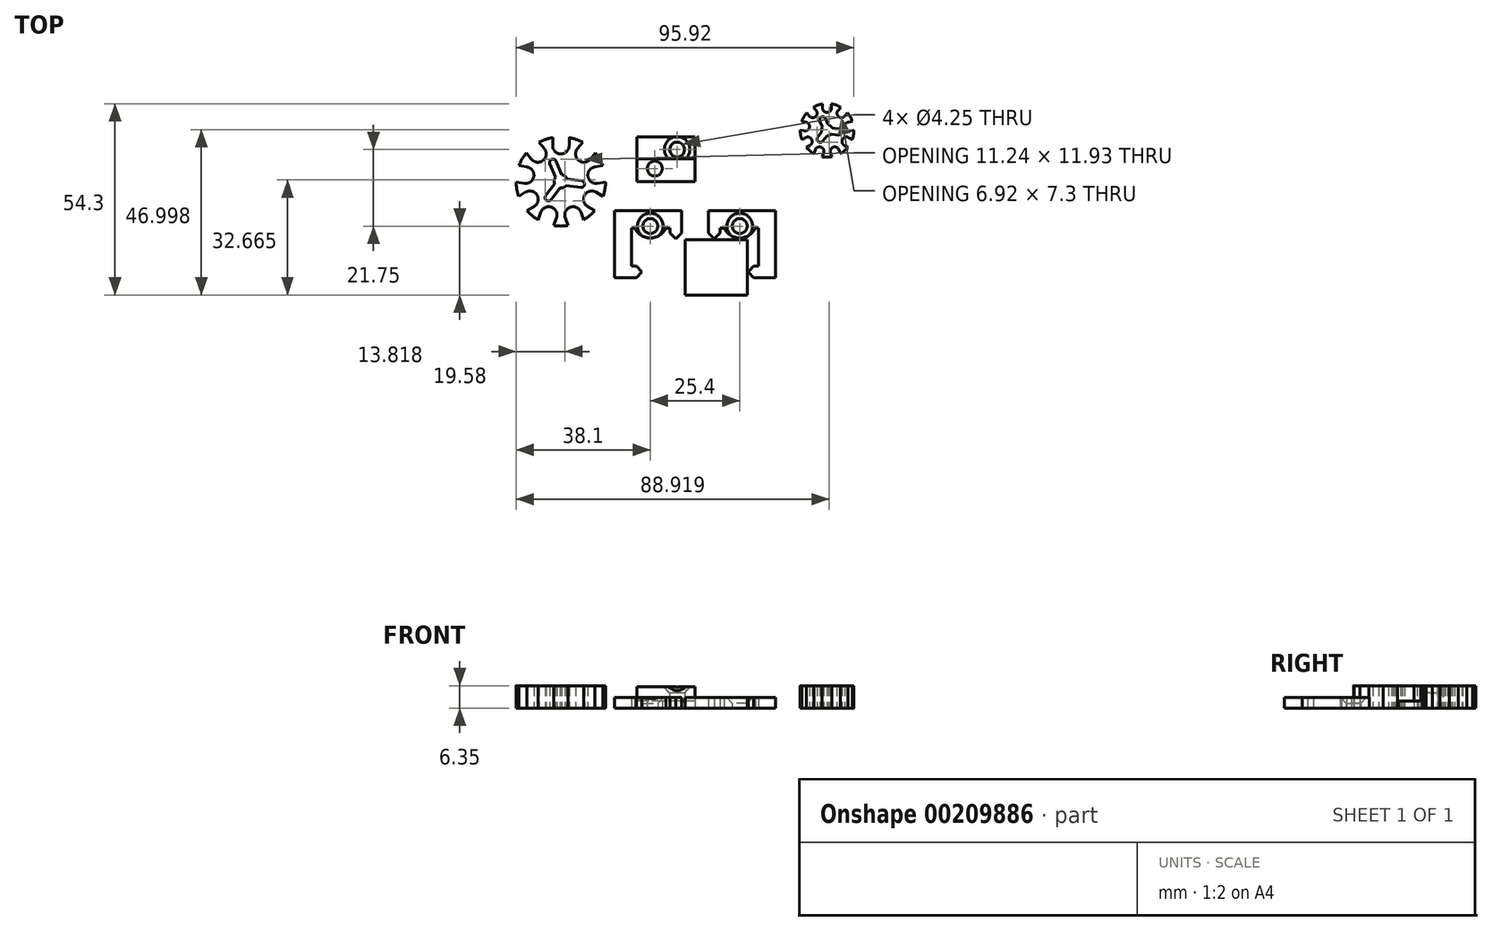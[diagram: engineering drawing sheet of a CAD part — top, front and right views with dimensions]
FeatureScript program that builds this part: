
annotation { "Feature Type Name" : "Feature", "Feature Type Description" : "" }
export const myFeature = defineFeature(function(context is Context, id is Id, definition is map)
    precondition{}
    {
        {
            var Q0;
            Q0=qCreatedBy(makeId("Top.planeOp"),FACE);
            var sketch = newSketch(context, id + "F0", { "sketchPlane" : qUnion([Q0])});
            skLineSegment(sketch, "E0.bottom", {"start": v(0, 0) * mm, "end": v(-16.51, 0) * mm});
            skLineSegment(sketch, "E0.top", {"start": v(0, 12.7) * mm, "end": v(-16.51, 12.7) * mm});
            skLineSegment(sketch, "E0.left", {"start": v(0, 0) * mm, "end": v(0, 12.7) * mm});
            skLineSegment(sketch, "E0.right", {"start": v(-16.51, 0) * mm, "end": v(-16.51, 12.7) * mm});
            skCircle(sketch, "E1", {"center": v(-11.43, 3.65) * mm, "radius": 2.12 * mm});
            skCircle(sketch, "E2", {"center": v(-5.08, 9.05) * mm, "radius": 2.12 * mm});
            skLineSegment(sketch, "E3", {"start": v(-11.43, 3.65) * mm, "end": v(-5.08, 3.65) * mm, "construction": true});
            skLineSegment(sketch, "E4", {"start": v(-5.08, 3.65) * mm, "end": v(-5.08, 9.05) * mm, "construction": true});
            skLineSegment(sketch, "E5", {"start": v(-16.51, 6.35) * mm, "end": v(0, 6.35) * mm, "construction": true});
            skPoint(sketch, "E6", {"position": v(-5.08, 6.35) * mm});
            skLineSegment(sketch, "E7", {"start": v(-5.08, 3.65) * mm, "end": v(0, 3.65) * mm, "construction": true});
            skLineSegment(sketch, "E8", {"start": v(-5.08, 3.65) * mm, "end": v(-5.08, 0) * mm, "construction": true});
            skLineSegment(sketch, "E9", {"start": v(-5.08, 9.05) * mm, "end": v(-5.08, 12.7) * mm, "construction": true});
            skPoint(sketch, "E10", {"position": v(-8.26, 3.65) * mm});
            skPoint(sketch, "E11", {"position": v(-8.26, 0) * mm});
            skSolve(sketch);
        }
        {
            var Q0;
            Q0 = qSketchRegion(id + "F0", true);
            extrude(context, id + "F1", {"entities" : qUnion([Q0]), "depth" : 2 * mm});
        }
        {
            var Q0;
            Q0=makeQuery(id+"F1.opExtrude","CAP_FACE",FACE,{"disambiguationData":[OSD([sQuery(id+"F0.wireOp",EDGE,"E0.bottom"),sQuery(id+"F0.wireOp",EDGE,"E0.top"),sQuery(id+"F0.wireOp",EDGE,"E0.left"),sQuery(id+"F0.wireOp",EDGE,"E0.right"),sQuery(id+"F0.wireOp",EDGE,"E1"),sQuery(id+"F0.wireOp",EDGE,"E2")])],"isStart":false});
            var sketch = newSketch(context, id + "F2", { "sketchPlane" : qUnion([Q0])});
            skLineSegment(sketch, "E12.bottom", {"start": v(0, 0) * mm, "end": v(-16.51, 0) * mm});
            skLineSegment(sketch, "E12.top", {"start": v(0, 6.4) * mm, "end": v(-16.51, 6.4) * mm});
            skLineSegment(sketch, "E12.left", {"start": v(0, 0) * mm, "end": v(0, 6.4) * mm});
            skLineSegment(sketch, "E12.right", {"start": v(-16.51, 0) * mm, "end": v(-16.51, 6.4) * mm});
            skCircle(sketch, "E13", {"center": v(-11.43, 3.65) * mm, "radius": 1.48 * mm, "construction": true});
            skSolve(sketch);
        }
        {
            var Q0;
            {var subQ2=sQuery(id+"F2.wireOp",EDGE,"E12.top");Q0=makeQuery(id+"F2.imprint","IMPRINT",FACE,{"disambiguationData":[TD([[makeQuery(id+"F2.imprint","IMPRINT",EDGE,{"derivedFrom":subQ2}),-1.0]])]});}
            extrude(context, id + "F3", {"entities" : qUnion([Q0]), "operationType" : NewBodyOperationType.ADD, "depth" : 4 * mm});
        }
        {
            var Q0;
            Q0=qCreatedBy(makeId("Top.planeOp"),FACE);
            var sketch = newSketch(context, id + "F4", { "sketchPlane" : qUnion([Q0])});
            skCircle(sketch, "E14", {"center": v(12.7, -12.7) * mm, "radius": 2.12 * mm});
            skLineSegment(sketch, "E15.bottom", {"start": v(14.83, -16.51) * mm, "end": v(-2.84, -16.5) * mm});
            skLineSegment(sketch, "E15.top", {"start": v(14.83, -32.28) * mm, "end": v(-2.84, -32.28) * mm});
            skLineSegment(sketch, "E15.left", {"start": v(14.83, -16.5) * mm, "end": v(14.83, -32.28) * mm});
            skLineSegment(sketch, "E15.right", {"start": v(-2.84, -16.51) * mm, "end": v(-2.84, -32.28) * mm});
            skLineSegment(sketch, "E16", {"start": v(22.9, -8.25) * mm, "end": v(22.9, -27.3) * mm});
            skLineSegment(sketch, "E17", {"start": v(22.9, -27.3) * mm, "end": v(16.68, -27.3) * mm});
            skLineSegment(sketch, "E18", {"start": v(16.68, -27.3) * mm, "end": v(15.08, -25.7) * mm});
            skLineSegment(sketch, "E19", {"start": v(15.08, -25.7) * mm, "end": v(16.68, -24.1) * mm});
            skLineSegment(sketch, "E20", {"start": v(16.68, -24.1) * mm, "end": v(18.08, -24.1) * mm});
            skLineSegment(sketch, "E21", {"start": v(18.08, -24.1) * mm, "end": v(18.08, -13.26) * mm});
            skLineSegment(sketch, "E22", {"start": v(18.08, -13.26) * mm, "end": v(7.05, -13.26) * mm});
            skLineSegment(sketch, "E23", {"start": v(3.85, -17.14) * mm, "end": v(3.85, -8.25) * mm});
            skLineSegment(sketch, "E24", {"start": v(7.05, -13.26) * mm, "end": v(3.85, -13.26) * mm, "construction": true});
            skLineSegment(sketch, "E25", {"start": v(18.08, -24.1) * mm, "end": v(18.08, -27.3) * mm, "construction": true});
            skLineSegment(sketch, "E26", {"start": v(3.85, -12.7) * mm, "end": v(22.9, -12.7) * mm, "construction": true});
            skArc(sketch, "E27", {"start": v(8.26, -13.26) * mm, "mid": v(12.7, -16.07) * mm, "end": v(17.15, -13.26) * mm});
            skArc(sketch, "E28", {"start": v(17.15, -12.14) * mm, "mid": v(12.7, -9.33) * mm, "end": v(8.26, -12.14) * mm});
            skLineSegment(sketch, "E29", {"start": v(8.26, -12.14) * mm, "end": v(8.26, -12.7) * mm, "construction": true});
            skLineSegment(sketch, "E30", {"start": v(8.26, -13.26) * mm, "end": v(8.26, -12.7) * mm, "construction": true});
            skLineSegment(sketch, "E31", {"start": v(3.85, -8.25) * mm, "end": v(22.9, -8.25) * mm});
            skLineSegment(sketch, "E32", {"start": v(3.85, -14.65) * mm, "end": v(3.85, -17.14) * mm});
            skLineSegment(sketch, "E33", {"start": v(3.85, -14.65) * mm, "end": v(5.45, -16.26) * mm});
            skLineSegment(sketch, "E34", {"start": v(5.45, -16.26) * mm, "end": v(7.05, -14.65) * mm});
            skLineSegment(sketch, "E35", {"start": v(7.05, -14.65) * mm, "end": v(7.05, -13.26) * mm});
            skSolve(sketch);
        }
        {
            var Q0;
            Q0=makeQuery(id+"F4.imprint","IMPRINT",FACE,{"disambiguationData":[TD([[makeQuery(id+"F4.imprint","IMPRINT",EDGE,{"derivedFrom":sQuery(id+"F4.wireOp",EDGE,"E14")}),-1.0]])]});
            var Q1;
            Q1=makeQuery(id+"F4.imprint","IMPRINT",FACE,{"disambiguationData":[TD([[makeQuery(id+"F4.imprint","IMPRINT",EDGE,{"derivedFrom":sQuery(id+"F4.wireOp",EDGE,"E15.bottom")}),1.0]])]});
            var Q2;
            Q2=makeQuery(id+"F4.imprint","IMPRINT",FACE,{"disambiguationData":[TD([[makeQuery(id+"F4.imprint","IMPRINT",EDGE,{"derivedFrom":sQuery(id+"F4.wireOp",EDGE,"zlfB7uTj-bSs5-uBsl-dvmD-jEP82ZwISSBb")}),-1.0]])]});
            var Q3;
            {var subQ0=sQuery(id+"F4.wireOp",EDGE,"E28");var subQ1=sQuery(id+"F4.wireOp",EDGE,"zlfB7uTj-bSs5-uBsl-dvmD-jEP82ZwISSBb");var subQ2=makeQuery(id+"F4.imprint","INTERSECT",VERTEX,{"disambiguationData":[OD(0.0)],"derivedFrom":[subQ1,subQ0]});Q3=makeQuery(id+"F4.imprint","IMPRINT",FACE,{"disambiguationData":[TD([[makeQuery(id+"F4.imprint","IMPRINT",EDGE,{"disambiguationData":[TD([[subQ2,-1.0]])],"derivedFrom":subQ1}),1.0]])]});}
            var Q4;
            {var subQ3=sQuery(id+"F4.wireOp",EDGE,"E16");Q4=makeQuery(id+"F4.imprint","IMPRINT",FACE,{"disambiguationData":[TD([[makeQuery(id+"F4.imprint","IMPRINT",EDGE,{"derivedFrom":subQ3}),-1.0]])]});}
            extrude(context, id + "F5", {"entities" : qUnion([Q0, Q1, Q2, Q3, Q4]), "depth" : 3 * mm});
        }
        {
            var Q0;
            Q0=makeQuery(id+"F5.opExtrude","SWEPT_FACE",FACE,{"disambiguationData":[OSD([sQuery(id+"F4.wireOp",EDGE,"E31")])]});
            cPlane(context, id + "F6", {"entities" : qUnion([Q0]), "cplaneType" : CPlaneType.OFFSET, "offset" : 4.44 * mm, "oppositeDirection" : true, "width" : 152.4 * mm, "height" : 152.4 * mm});
        }
        {
            var Q0;
            Q0=qCreatedBy(id+"F6.planeOp",FACE);
            var sketch = newSketch(context, id + "F7", { "sketchPlane" : qUnion([Q0])});
            skLineSegment(sketch, "E36", {"start": v(-12.7, 3) * mm, "end": v(-12.7, -0.4) * mm, "construction": true});
            skLineSegment(sketch, "E37", {"start": v(-12.7, 3) * mm, "end": v(-16.35, 3) * mm});
            skLineSegment(sketch, "E38", {"start": v(-16.35, 3) * mm, "end": v(-14.6, 1.1) * mm});
            skLineSegment(sketch, "E39", {"start": v(-14.6, 1.1) * mm, "end": v(-12.7, 1.1) * mm});
            skLineSegment(sketch, "E40", {"start": v(-12.7, 1.1) * mm, "end": v(-12.7, 3) * mm});
            skLineSegment(sketch, "E41.MirrorCS", {"start": v(-12.7, 3) * mm, "end": v(-9.05, 3) * mm, "construction": true});
            skLineSegment(sketch, "E42.MirrorCS", {"start": v(-9.05, 3) * mm, "end": v(-10.8, 1.1) * mm, "construction": true});
            skLineSegment(sketch, "E43.MirrorCS", {"start": v(-10.8, 1.1) * mm, "end": v(-12.7, 1.1) * mm, "construction": true});
            skSolve(sketch);
        }
        {
            var Q0;
            Q0 = qSketchRegion(id + "F7", true);
            var Q1;
            Q1=sQuery(id+"F7.wireOp",EDGE,"E40");
            revolve(context, id + "F8", {"operationType" : NewBodyOperationType.REMOVE, "entities" : qUnion([Q0]), "axis" : qUnion([Q1]), "revolveType" : RevolveType.FULL, "oppositeDirection" : true});
        }
        {
            var Q0;
            Q0=makeQuery(id+"F5.opExtrude","SWEPT_BODY",BODY,{"disambiguationData":[OSD([sQuery(id+"F4.wireOp",EDGE,"E14"),sQuery(id+"F4.wireOp",EDGE,"zlfB7uTj-bSs5-uBsl-dvmD-jEP82ZwISSBb"),sQuery(id+"F4.wireOp",EDGE,"E16"),sQuery(id+"F4.wireOp",EDGE,"E17"),sQuery(id+"F4.wireOp",EDGE,"E18"),sQuery(id+"F4.wireOp",EDGE,"E19"),sQuery(id+"F4.wireOp",EDGE,"E20"),sQuery(id+"F4.wireOp",EDGE,"E21"),sQuery(id+"F4.wireOp",EDGE,"E22"),sQuery(id+"F4.wireOp",EDGE,"cID7fQ1h-tPc6-9q32-Ci6z-0261RFLuPbeZ"),sQuery(id+"F4.wireOp",EDGE,"jHLlkeLY-MZKs-cIrp-9K9G-fC4B7sUc40gJ"),sQuery(id+"F4.wireOp",EDGE,"MUQYEYnl-2blG-JDVs-KfyZ-8IninS7B80Zu"),sQuery(id+"F4.wireOp",EDGE,"E23")])]});
            var Q1;
            Q1=qCreatedBy(makeId("Right.planeOp"),FACE);
            mirror(context, id + "F9", {"entities" : qUnion([Q0]), "mirrorPlane" : qUnion([Q1])});
        }
        {
            var Q0;
            Q0=makeQuery(id+"F3.opExtrude","SWEPT_FACE",FACE,{"disambiguationData":[OSD([sQuery(id+"F2.wireOp",EDGE,"E12.top")])]});
            cPlane(context, id + "F10", {"entities" : qUnion([Q0]), "cplaneType" : CPlaneType.OFFSET, "offset" : 2.7 * mm, "oppositeDirection" : true, "width" : 152.4 * mm, "height" : 152.4 * mm});
        }
        {
            var Q0;
            Q0=qCreatedBy(id+"F10.planeOp",FACE);
            var sketch = newSketch(context, id + "F11", { "sketchPlane" : qUnion([Q0])});
            skLineSegment(sketch, "E44", {"start": v(-5.08, 6) * mm, "end": v(-5.08, 3.17) * mm, "construction": true});
            skLineSegment(sketch, "E45", {"start": v(-5.08, 6) * mm, "end": v(-8.7, 6) * mm});
            skLineSegment(sketch, "E46", {"start": v(-8.7, 6) * mm, "end": v(-6.99, 4.1) * mm});
            skLineSegment(sketch, "E47", {"start": v(-6.99, 4.1) * mm, "end": v(-5.08, 4.1) * mm});
            skLineSegment(sketch, "E48", {"start": v(-5.08, 4.1) * mm, "end": v(-5.08, 6) * mm});
            skLineSegment(sketch, "E49.MirrorCS", {"start": v(-5.08, 6) * mm, "end": v(-1.46, 6) * mm, "construction": true});
            skLineSegment(sketch, "E50.MirrorCS", {"start": v(-1.46, 6) * mm, "end": v(-3.18, 4.1) * mm, "construction": true});
            skLineSegment(sketch, "E51.MirrorCS", {"start": v(-3.18, 4.1) * mm, "end": v(-5.08, 4.1) * mm, "construction": true});
            skSolve(sketch);
        }
        {
            var Q0;
            Q0 = qSketchRegion(id + "F11", true);
            var Q1;
            Q1=sQuery(id+"F11.wireOp",EDGE,"E44");
            revolve(context, id + "F12", {"operationType" : NewBodyOperationType.REMOVE, "entities" : qUnion([Q0]), "axis" : qUnion([Q1]), "revolveType" : RevolveType.FULL, "oppositeDirection" : true});
        }
        {
            var Q0;
            Q0=qCreatedBy(makeId("Top.planeOp"),FACE);
            var sketch = newSketch(context, id + "F13", { "sketchPlane" : qUnion([Q0])});
            skCircle(sketch, "E52", {"center": v(-38.1, 0) * mm, "radius": 12.7 * mm});
            skLineSegment(sketch, "E53", {"start": v(-40.45, 12.48) * mm, "end": v(-40.45, 10.16) * mm});
            skLineSegment(sketch, "E54", {"start": v(-35.75, 12.48) * mm, "end": v(-35.75, 10.16) * mm});
            skArc(sketch, "E55", {"start": v(-40.45, 10.16) * mm, "mid": v(-38.1, 7.81) * mm, "end": v(-35.75, 10.16) * mm});
            skArc(sketch, "E56", {"start": v(-35.75, 12.48) * mm, "mid": v(-38.1, 12.7) * mm, "end": v(-40.45, 12.48) * mm});
            skLineSegment(sketch, "E57.1.1", {"start": v(-44.32, 11.07) * mm, "end": v(-42.83, 9.3) * mm});
            skArc(sketch, "E57.1.2", {"start": v(-46.43, 6.27) * mm, "mid": v(-43.12, 5.98) * mm, "end": v(-42.83, 9.3) * mm});
            skLineSegment(sketch, "E57.1.3", {"start": v(-47.92, 8.05) * mm, "end": v(-46.43, 6.27) * mm});
            skLineSegment(sketch, "E57.2.1", {"start": v(-49.98, 4.48) * mm, "end": v(-47.7, 4.08) * mm});
            skArc(sketch, "E57.2.2", {"start": v(-48.51, -0.55) * mm, "mid": v(-45.8, 1.36) * mm, "end": v(-47.7, 4.08) * mm});
            skLineSegment(sketch, "E57.2.3", {"start": v(-50.8, -0.15) * mm, "end": v(-48.51, -0.55) * mm});
            skLineSegment(sketch, "E57.3.1", {"start": v(-50.08, -4.2) * mm, "end": v(-48.07, -3.05) * mm});
            skArc(sketch, "E57.3.2", {"start": v(-45.72, -7.11) * mm, "mid": v(-44.86, -3.9) * mm, "end": v(-48.07, -3.05) * mm});
            skLineSegment(sketch, "E57.3.3", {"start": v(-47.73, -8.28) * mm, "end": v(-45.72, -7.11) * mm});
            skLineSegment(sketch, "E57.4.1", {"start": v(-44.58, -10.92) * mm, "end": v(-43.78, -8.74) * mm});
            skArc(sketch, "E57.4.2", {"start": v(-39.37, -10.35) * mm, "mid": v(-40.77, -7.34) * mm, "end": v(-43.78, -8.74) * mm});
            skLineSegment(sketch, "E57.4.3", {"start": v(-40.16, -12.53) * mm, "end": v(-39.37, -10.35) * mm});
            skLineSegment(sketch, "E57.5.1", {"start": v(-36.04, -12.53) * mm, "end": v(-36.83, -10.35) * mm});
            skArc(sketch, "E57.5.2", {"start": v(-32.42, -8.74) * mm, "mid": v(-35.43, -7.34) * mm, "end": v(-36.83, -10.35) * mm});
            skLineSegment(sketch, "E57.5.3", {"start": v(-31.62, -10.92) * mm, "end": v(-32.42, -8.74) * mm});
            skLineSegment(sketch, "E57.6.1", {"start": v(-28.47, -8.28) * mm, "end": v(-30.48, -7.11) * mm});
            skArc(sketch, "E57.6.2", {"start": v(-28.13, -3.05) * mm, "mid": v(-31.34, -3.9) * mm, "end": v(-30.48, -7.11) * mm});
            skLineSegment(sketch, "E57.6.3", {"start": v(-26.12, -4.2) * mm, "end": v(-28.13, -3.05) * mm});
            skLineSegment(sketch, "E57.7.1", {"start": v(-25.4, -0.15) * mm, "end": v(-27.69, -0.55) * mm});
            skArc(sketch, "E57.7.2", {"start": v(-28.5, 4.08) * mm, "mid": v(-30.4, 1.36) * mm, "end": v(-27.69, -0.55) * mm});
            skLineSegment(sketch, "E57.7.3", {"start": v(-26.22, 4.48) * mm, "end": v(-28.5, 4.08) * mm});
            skCircle(sketch, "E58", {"center": v(-38.1, 0) * mm, "radius": 1.9 * mm});
            skLineSegment(sketch, "E59", {"start": v(-39.61, 1.16) * mm, "end": v(-41.22, 5.03) * mm});
            skLineSegment(sketch, "E60", {"start": v(-41.22, 5.03) * mm, "end": v(-39.46, 5.76) * mm});
            skLineSegment(sketch, "E61", {"start": v(-39.46, 5.76) * mm, "end": v(-37.85, 1.89) * mm});
            skPoint(sketch, "E62", {"position": v(-40.34, 5.4) * mm});
            skLineSegment(sketch, "E63", {"start": v(-40.34, 5.4) * mm, "end": v(-38.1, 0) * mm, "construction": true});
            skLineSegment(sketch, "E64", {"start": v(-39.22, 2.7) * mm, "end": v(-40.1, 2.33) * mm, "construction": true});
            skLineSegment(sketch, "E65", {"start": v(-39.22, 2.7) * mm, "end": v(-38.34, 3.06) * mm, "construction": true});
            skLineSegment(sketch, "E66", {"start": v(-50.8, 0) * mm, "end": v(-25.4, 0) * mm, "construction": true});
            skArc(sketch, "E67", {"start": v(-39.46, 5.76) * mm, "mid": v(-40.7, 6.28) * mm, "end": v(-41.22, 5.03) * mm});
            skLineSegment(sketch, "E68.1.0", {"start": v(-38.35, -1.89) * mm, "end": v(-40.9, -5.21) * mm});
            skArc(sketch, "E68.1.1", {"start": v(-42.41, -4.05) * mm, "mid": v(-42.24, -5.39) * mm, "end": v(-40.9, -5.21) * mm});
            skLineSegment(sketch, "E68.1.2", {"start": v(-42.41, -4.05) * mm, "end": v(-39.86, -0.73) * mm});
            skLineSegment(sketch, "E68.2.0", {"start": v(-36.34, 0.73) * mm, "end": v(-32.18, 0.18) * mm});
            skArc(sketch, "E68.2.1", {"start": v(-32.43, -1.7) * mm, "mid": v(-31.36, -0.89) * mm, "end": v(-32.18, 0.18) * mm});
            skLineSegment(sketch, "E68.2.2", {"start": v(-32.43, -1.7) * mm, "end": v(-36.59, -1.16) * mm});
            skLineSegment(sketch, "E69.2.8.0", {"start": v(-28.28, 8.05) * mm, "end": v(-29.77, 6.27) * mm});
            skArc(sketch, "E69.5.8.0", {"start": v(-33.37, 9.3) * mm, "mid": v(-33.08, 5.98) * mm, "end": v(-29.77, 6.27) * mm});
            skLineSegment(sketch, "E69.9.8.0", {"start": v(-31.88, 11.07) * mm, "end": v(-33.37, 9.3) * mm});
            skCircle(sketch, "E70", {"center": v(37.5, 14.5) * mm, "radius": 7.62 * mm});
            skLineSegment(sketch, "E71", {"start": v(36.23, 22.02) * mm, "end": v(36.23, 20.85) * mm});
            skLineSegment(sketch, "E72", {"start": v(38.77, 22.02) * mm, "end": v(38.77, 20.85) * mm});
            skArc(sketch, "E73", {"start": v(36.23, 20.85) * mm, "mid": v(37.5, 19.58) * mm, "end": v(38.77, 20.85) * mm});
            skArc(sketch, "E74", {"start": v(38.77, 22.02) * mm, "mid": v(37.5, 22.12) * mm, "end": v(36.23, 22.02) * mm});
            skLineSegment(sketch, "E75.1.1", {"start": v(33.65, 21.08) * mm, "end": v(34.4, 20.18) * mm});
            skArc(sketch, "E75.1.2", {"start": v(32.45, 18.55) * mm, "mid": v(34.24, 18.4) * mm, "end": v(34.4, 20.18) * mm});
            skLineSegment(sketch, "E75.1.3", {"start": v(31.7, 19.44) * mm, "end": v(32.45, 18.55) * mm});
            skLineSegment(sketch, "E75.2.1", {"start": v(30.32, 17.06) * mm, "end": v(31.47, 16.86) * mm});
            skArc(sketch, "E75.2.2", {"start": v(31.03, 14.36) * mm, "mid": v(32.5, 15.39) * mm, "end": v(31.47, 16.86) * mm});
            skLineSegment(sketch, "E75.2.3", {"start": v(29.88, 14.56) * mm, "end": v(31.03, 14.36) * mm});
            skLineSegment(sketch, "E75.3.1", {"start": v(30.36, 11.85) * mm, "end": v(31.37, 12.43) * mm});
            skArc(sketch, "E75.3.2", {"start": v(32.64, 10.23) * mm, "mid": v(33.1, 11.96) * mm, "end": v(31.37, 12.43) * mm});
            skLineSegment(sketch, "E75.3.3", {"start": v(31.63, 9.65) * mm, "end": v(32.64, 10.23) * mm});
            skLineSegment(sketch, "E75.4.1", {"start": v(33.74, 7.88) * mm, "end": v(34.14, 8.97) * mm});
            skArc(sketch, "E75.4.2", {"start": v(36.52, 8.1) * mm, "mid": v(35.77, 9.73) * mm, "end": v(34.14, 8.97) * mm});
            skLineSegment(sketch, "E75.4.3", {"start": v(36.13, 7) * mm, "end": v(36.52, 8.1) * mm});
            skLineSegment(sketch, "E75.5.1", {"start": v(38.88, 7) * mm, "end": v(38.48, 8.1) * mm});
            skArc(sketch, "E75.5.2", {"start": v(40.87, 8.97) * mm, "mid": v(39.24, 9.73) * mm, "end": v(38.48, 8.1) * mm});
            skLineSegment(sketch, "E75.5.3", {"start": v(41.27, 7.88) * mm, "end": v(40.87, 8.97) * mm});
            skLineSegment(sketch, "E75.6.1", {"start": v(43.37, 9.65) * mm, "end": v(42.37, 10.23) * mm});
            skArc(sketch, "E75.6.2", {"start": v(43.64, 12.43) * mm, "mid": v(41.9, 11.96) * mm, "end": v(42.37, 10.23) * mm});
            skLineSegment(sketch, "E75.6.3", {"start": v(44.64, 11.85) * mm, "end": v(43.64, 12.43) * mm});
            skLineSegment(sketch, "E75.7.1", {"start": v(45.12, 14.56) * mm, "end": v(43.98, 14.36) * mm});
            skArc(sketch, "E75.7.2", {"start": v(43.54, 16.86) * mm, "mid": v(42.5, 15.39) * mm, "end": v(43.98, 14.36) * mm});
            skLineSegment(sketch, "E75.7.3", {"start": v(44.68, 17.06) * mm, "end": v(43.54, 16.86) * mm});
            skCircle(sketch, "E76", {"center": v(37.5, 14.5) * mm, "radius": 1.59 * mm});
            skLineSegment(sketch, "E77", {"start": v(36.18, 15.38) * mm, "end": v(35.45, 17.14) * mm});
            skLineSegment(sketch, "E78", {"start": v(35.45, 17.14) * mm, "end": v(37.1, 17.82) * mm});
            skLineSegment(sketch, "E79", {"start": v(37.1, 17.82) * mm, "end": v(37.82, 16.06) * mm});
            skPoint(sketch, "E80", {"position": v(36.27, 17.48) * mm});
            skLineSegment(sketch, "E81", {"start": v(36.27, 17.48) * mm, "end": v(37.5, 14.5) * mm, "construction": true});
            skLineSegment(sketch, "E82", {"start": v(36.89, 16) * mm, "end": v(36.07, 15.65) * mm, "construction": true});
            skLineSegment(sketch, "E83", {"start": v(36.89, 16) * mm, "end": v(37.7, 16.33) * mm, "construction": true});
            skLineSegment(sketch, "E84", {"start": v(29.88, 14.5) * mm, "end": v(45.12, 14.5) * mm, "construction": true});
            skArc(sketch, "E85", {"start": v(37.1, 17.82) * mm, "mid": v(35.93, 18.3) * mm, "end": v(35.45, 17.14) * mm});
            skLineSegment(sketch, "E86.1.0", {"start": v(37.4, 12.92) * mm, "end": v(36.25, 11.4) * mm});
            skArc(sketch, "E86.1.1", {"start": v(34.84, 12.5) * mm, "mid": v(35, 11.24) * mm, "end": v(36.25, 11.4) * mm});
            skLineSegment(sketch, "E86.1.2", {"start": v(34.84, 12.5) * mm, "end": v(36, 14) * mm});
            skLineSegment(sketch, "E86.2.0", {"start": v(38.92, 15.21) * mm, "end": v(40.81, 14.96) * mm});
            skArc(sketch, "E86.2.1", {"start": v(40.58, 13.2) * mm, "mid": v(41.58, 13.97) * mm, "end": v(40.81, 14.96) * mm});
            skLineSegment(sketch, "E86.2.2", {"start": v(40.58, 13.2) * mm, "end": v(38.7, 13.45) * mm});
            skLineSegment(sketch, "E87.2.8.0", {"start": v(43.3, 19.44) * mm, "end": v(42.56, 18.55) * mm});
            skArc(sketch, "E87.5.8.0", {"start": v(40.61, 20.18) * mm, "mid": v(40.77, 18.4) * mm, "end": v(42.56, 18.55) * mm});
            skLineSegment(sketch, "E87.9.8.0", {"start": v(41.36, 21.08) * mm, "end": v(40.61, 20.18) * mm});
            skSolve(sketch);
        }
        {
            var Q0;
            {var subQ15=sQuery(id+"F13.wireOp",EDGE,"E53");Q0=makeQuery(id+"F13.imprint","IMPRINT",FACE,{"disambiguationData":[TD([[makeQuery(id+"F13.imprint","IMPRINT",EDGE,{"derivedFrom":subQ15}),-1.0]])]});}
            var Q1;
            {var subQ7=sQuery(id+"F13.wireOp",EDGE,"E71");Q1=makeQuery(id+"F13.imprint","IMPRINT",FACE,{"disambiguationData":[TD([[makeQuery(id+"F13.imprint","IMPRINT",EDGE,{"derivedFrom":subQ7}),-1.0]])]});}
            extrude(context, id + "F14", {"entities" : qUnion([Q0, Q1]), "depth" : 6.35 * mm});
        }
    });
